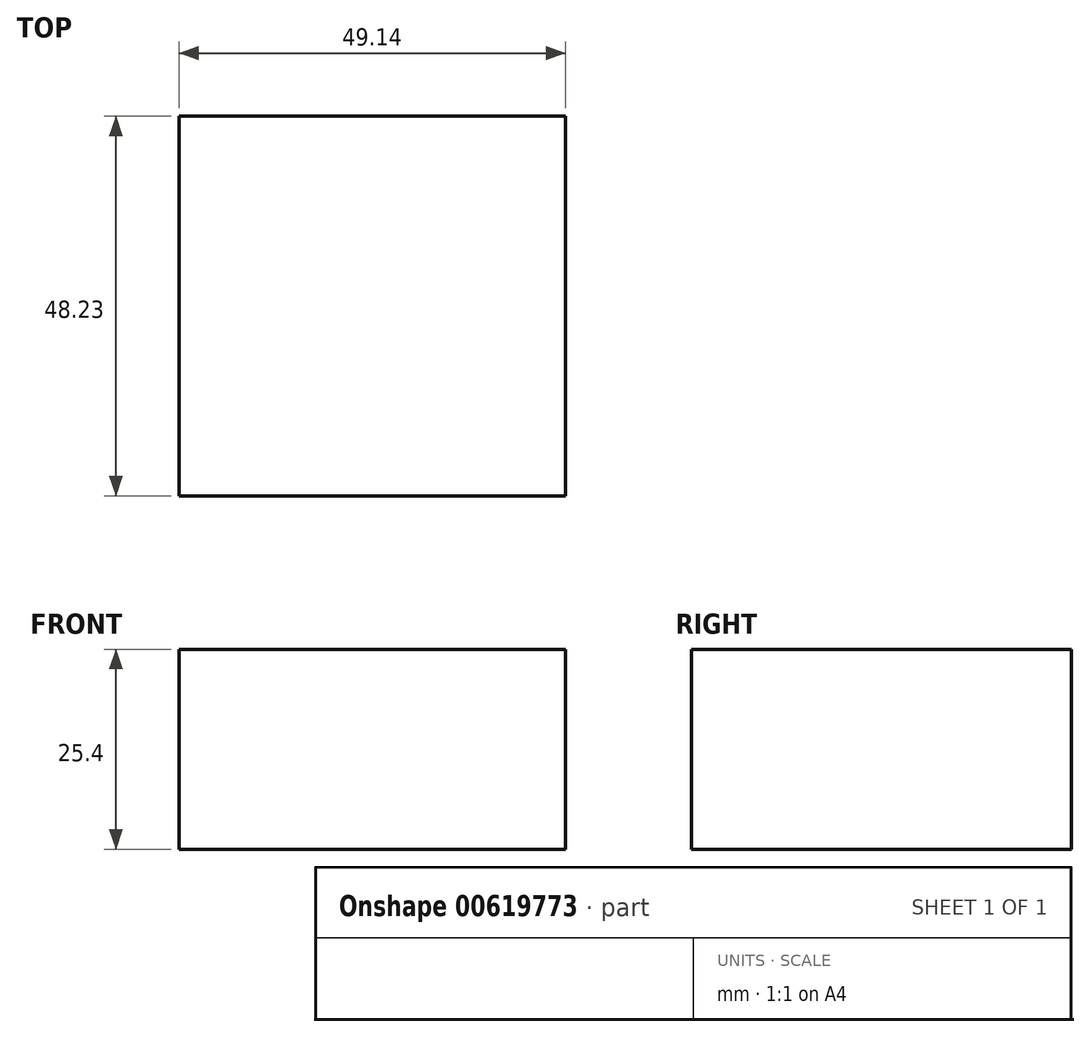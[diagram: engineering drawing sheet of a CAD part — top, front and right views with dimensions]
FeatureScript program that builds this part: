
annotation { "Feature Type Name" : "Feature", "Feature Type Description" : "" }
export const myFeature = defineFeature(function(context is Context, id is Id, definition is map)
    precondition{}
    {
        {
            var Q0;
            Q0=qCreatedBy(makeId("Top.planeOp"),FACE);
            var sketch = newSketch(context, id + "F0", { "sketchPlane" : qUnion([Q0])});
            skLineSegment(sketch, "E0.bottom", {"start": v(0, 0) * mm, "end": v(-49.14, 0) * mm});
            skLineSegment(sketch, "E0.top", {"start": v(0, -48.23) * mm, "end": v(-49.14, -48.23) * mm});
            skLineSegment(sketch, "E0.left", {"start": v(0, 0) * mm, "end": v(0, -48.23) * mm});
            skLineSegment(sketch, "E0.right", {"start": v(-49.14, 0) * mm, "end": v(-49.14, -48.23) * mm});
            skSolve(sketch);
        }
        {
            var Q0;
            Q0 = qSketchRegion(id + "F0", true);
            extrude(context, id + "F1", {"entities" : qUnion([Q0]), "depth" : 25.4 * mm, "offsetDistance" : 25.4 * mm});
        }
    });
